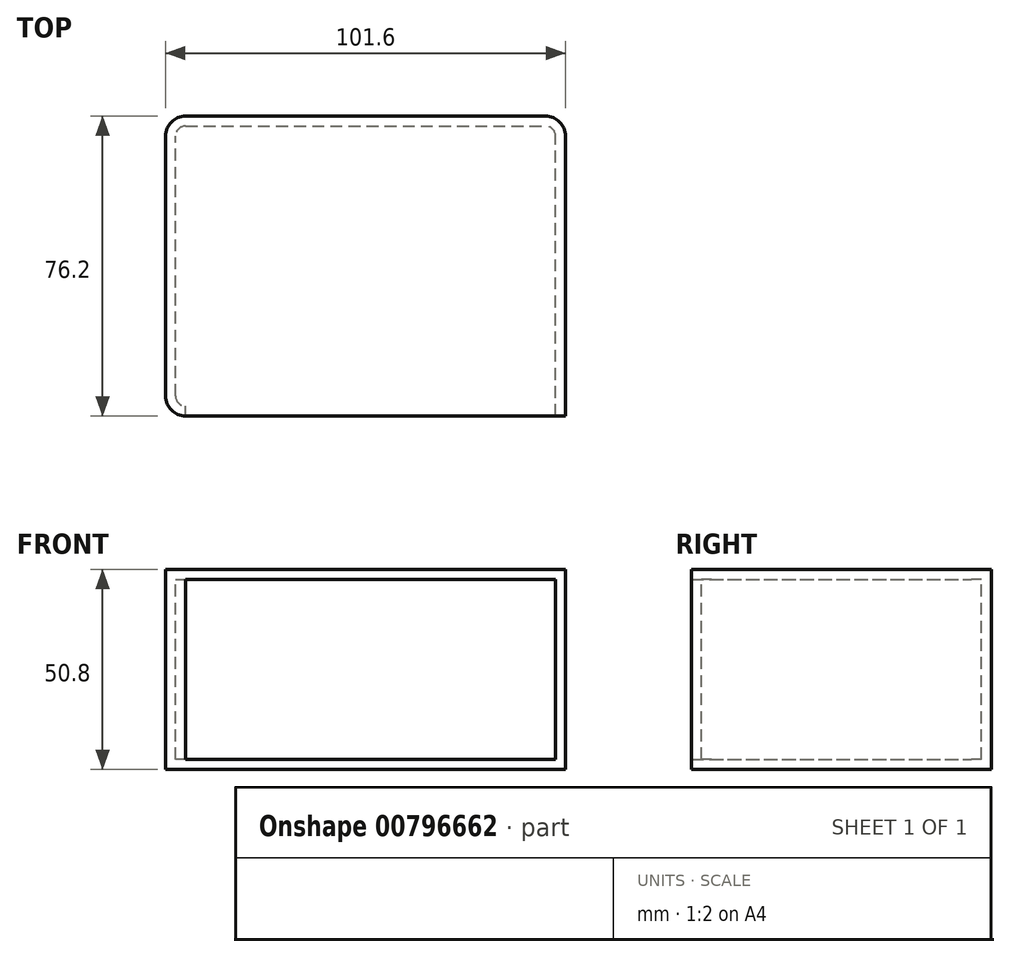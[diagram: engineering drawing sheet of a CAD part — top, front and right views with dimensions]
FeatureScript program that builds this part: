
annotation { "Feature Type Name" : "Feature", "Feature Type Description" : "" }
export const myFeature = defineFeature(function(context is Context, id is Id, definition is map)
    precondition{}
    {
        {
            var Q0;
            Q0=qCreatedBy(makeId("Front.planeOp"),FACE);
            var sketch = newSketch(context, id + "F0", { "sketchPlane" : qUnion([Q0])});
            skLineSegment(sketch, "E0.bottom", {"start": v(-39.37, 0) * mm, "end": v(62.23, 0) * mm});
            skLineSegment(sketch, "E0.top", {"start": v(-39.37, 50.8) * mm, "end": v(62.23, 50.8) * mm});
            skLineSegment(sketch, "E0.left", {"start": v(-39.37, 0) * mm, "end": v(-39.37, 50.8) * mm});
            skLineSegment(sketch, "E0.right", {"start": v(62.23, 0) * mm, "end": v(62.23, 50.8) * mm});
            skLineSegment(sketch, "E1.bottom", {"start": v(62.23, 0) * mm, "end": v(-39.37, 0) * mm});
            skLineSegment(sketch, "E1.top", {"start": v(62.23, 50.8) * mm, "end": v(-39.37, 50.8) * mm});
            skSolve(sketch);
        }
        {
            var Q0;
            Q0 = qSketchRegion(id + "F0", true);
            extrude(context, id + "F1", {"entities" : qUnion([Q0]), "depth" : 76.2 * mm, "offsetDistance" : 25.4 * mm});
        }
        {
            var Q0;
            Q0=makeQuery(id+"F1.opExtrude","CAP_EDGE",EDGE,{"disambiguationData":[OSD([sQuery(id+"F0.wireOp",EDGE,"E0.left")])],"isStart":false});
            var Q1;
            Q1=makeQuery(id+"F1.opExtrude","CAP_EDGE",EDGE,{"disambiguationData":[OSD([sQuery(id+"F0.wireOp",EDGE,"E0.left")])],"isStart":true});
            var Q2;
            Q2=makeQuery(id+"F1.opExtrude","CAP_EDGE",EDGE,{"disambiguationData":[OSD([sQuery(id+"F0.wireOp",EDGE,"E1.top")])],"isStart":true});
            var Q3;
            Q3=makeQuery(id+"F1.opExtrude","CAP_EDGE",EDGE,{"disambiguationData":[OSD([sQuery(id+"F0.wireOp",EDGE,"E0.right")])],"isStart":true});
            fillet(context, id + "F2", {"entities" : qUnion([Q0, Q1, Q2, Q3]), "radius" : 5.08 * mm, "tangentPropagation" : true, "allowEdgeOverflow" : false});
        }
        {
            var Q0;
            Q0=makeQuery(id+"F1.opExtrude","CAP_FACE",FACE,{"disambiguationData":[OSD([sQuery(id+"F0.wireOp",EDGE,"E1.bottom"),sQuery(id+"F0.wireOp",EDGE,"E1.top"),sQuery(id+"F0.wireOp",EDGE,"E0.right"),sQuery(id+"F0.wireOp",EDGE,"E0.left")])],"isStart":false});
            shell(context, id + "F3", {"entities" : qUnion([Q0]), "thickness" : 2.54 * mm});
        }
    });
